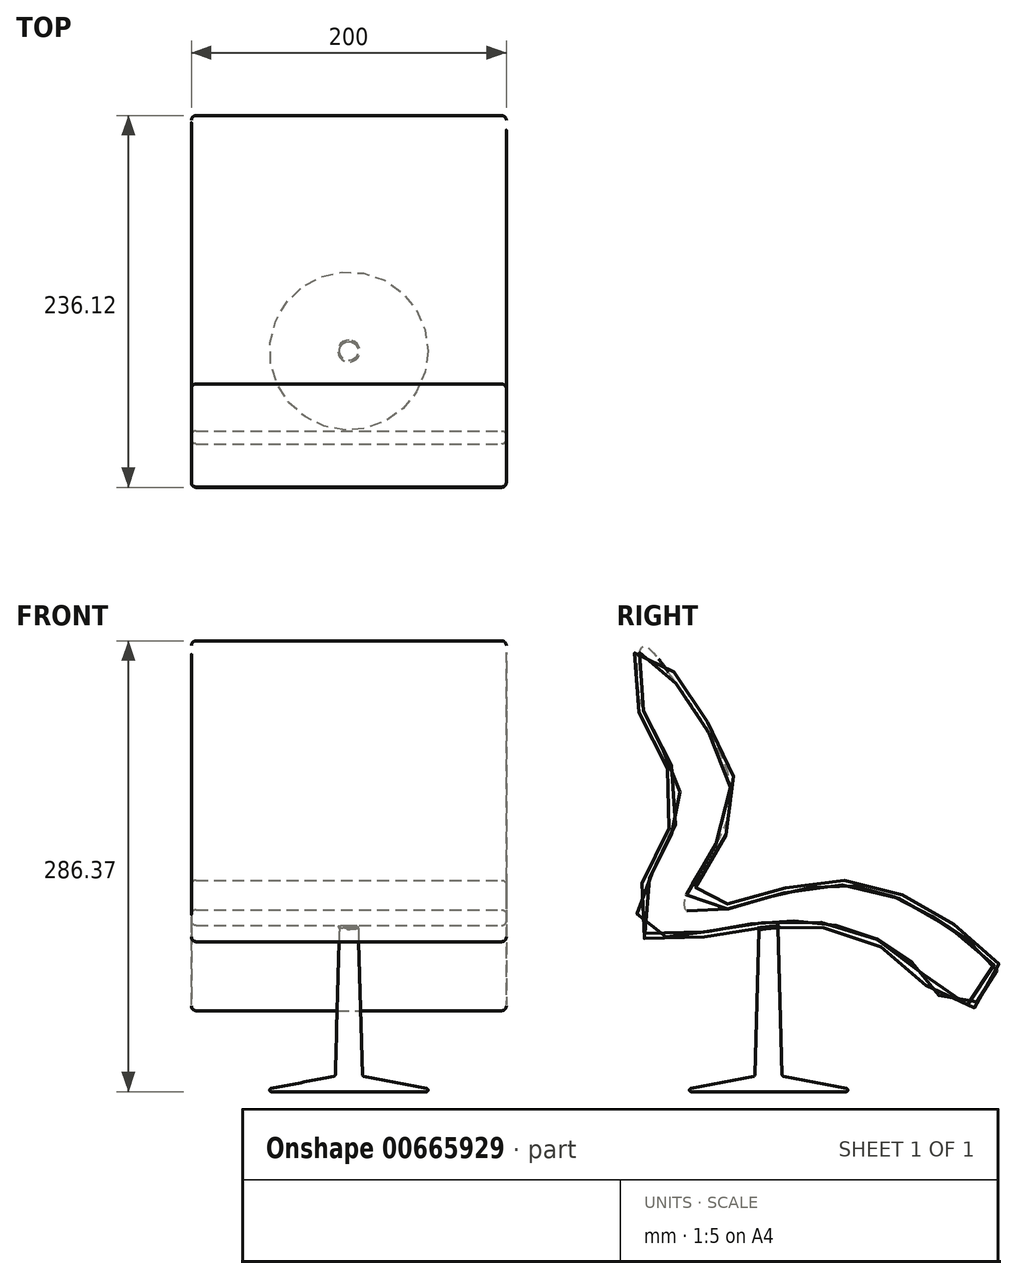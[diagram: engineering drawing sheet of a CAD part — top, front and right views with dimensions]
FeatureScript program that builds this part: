
annotation { "Feature Type Name" : "Feature", "Feature Type Description" : "" }
export const myFeature = defineFeature(function(context is Context, id is Id, definition is map)
    precondition{}
    {
        {
            var Q0;
            Q0=qCreatedBy(makeId("Top.planeOp"),FACE);
            var sketch = newSketch(context, id + "F0", { "sketchPlane" : qUnion([Q0])});
            skCircle(sketch, "E0", {"center": v(0, 0) * mm, "radius": 59.53 * mm});
            skSolve(sketch);
        }
        {
            var Q0;
            Q0=qCreatedBy(makeId("Top.planeOp"),FACE);
            cPlane(context, id + "F1", {"entities" : qUnion([Q0]), "cplaneType" : CPlaneType.OFFSET, "offset" : 10 * mm, "width" : 150 * mm, "height" : 150 * mm});
        }
        {
            var Q0;
            Q0=qCreatedBy(id+"F1.planeOp",FACE);
            var sketch = newSketch(context, id + "F2", { "sketchPlane" : qUnion([Q0])});
            skCircle(sketch, "E1", {"center": v(0, 0) * mm, "radius": 8.68 * mm});
            skSolve(sketch);
        }
        {
            var Q0;
            Q0=makeQuery(id+"F0.imprint","IMPRINT",FACE,{"disambiguationData":[TD([[makeQuery(id+"F0.imprint","IMPRINT",EDGE,{"derivedFrom":sQuery(id+"F0.wireOp",EDGE,"E0")}),1.0]])]});
            var Q1;
            Q1=makeQuery(id+"F2.imprint","IMPRINT",FACE,{"disambiguationData":[TD([[makeQuery(id+"F2.imprint","IMPRINT",EDGE,{"derivedFrom":sQuery(id+"F2.wireOp",EDGE,"E1")}),1.0]])]});
            loft(context, id + "F3", {"sheetProfilesArray" : [{ "sheetProfileEntities" : qUnion([Q0]) }, { "sheetProfileEntities" : qUnion([Q1]) }]});
        }
        {
            var Q0;
            Q0=qCreatedBy(id+"F1.planeOp",FACE);
            cPlane(context, id + "F4", {"entities" : qUnion([Q0]), "cplaneType" : CPlaneType.OFFSET, "offset" : 100 * mm, "width" : 150 * mm, "height" : 150 * mm});
        }
        {
            var Q0;
            Q0=qCreatedBy(id+"F4.planeOp",FACE);
            var sketch = newSketch(context, id + "F5", { "sketchPlane" : qUnion([Q0])});
            skCircle(sketch, "E2", {"center": v(0, 0) * mm, "radius": 5.83 * mm});
            skSolve(sketch);
        }
        {
            var Q0;
            Q0=qCreatedBy(id+"F1.planeOp",FACE);
            var sketch = newSketch(context, id + "F6", { "sketchPlane" : qUnion([Q0])});
            skCircle(sketch, "E3", {"center": v(0, 0) * mm, "radius": 8.62 * mm});
            skSolve(sketch);
        }
        {
            var Q1;
            Q1=makeQuery(id+"F6.imprint","IMPRINT",FACE,{"disambiguationData":[TD([[makeQuery(id+"F6.imprint","IMPRINT",EDGE,{"derivedFrom":sQuery(id+"F6.wireOp",EDGE,"E3")}),1.0]])]});
            var Q2;
            Q2=makeQuery(id+"F5.imprint","IMPRINT",FACE,{"disambiguationData":[TD([[makeQuery(id+"F5.imprint","IMPRINT",EDGE,{"derivedFrom":sQuery(id+"F5.wireOp",EDGE,"E2")}),1.0]])]});
            loft(context, id + "F7", {"operationType" : NewBodyOperationType.ADD, "sheetProfilesArray" : [{ "sheetProfileEntities" : qUnion([Q1]) }, { "sheetProfileEntities" : qUnion([Q2]) }]});
        }
        {
            var Q0;
            Q0=makeQuery(id+"F7.opLoft","SWEPT_FACE",FACE,{"disambiguationData":[OSD([sQuery(id+"F5.wireOp",EDGE,"E2"),sQuery(id+"F6.wireOp",EDGE,"E3")])]});
            fillet(context, id + "F8", {"entities" : qUnion([Q0]), "radius" : 1 * mm, "tangentPropagation" : true, "allowEdgeOverflow" : false});
        }
        {
            var Q0;
            Q0=makeQuery(id+"F3.opLoft","MID_CAP_EDGE",EDGE,{"disambiguationData":[OSD([sQuery(id+"F0.wireOp",EDGE,"E0")])],"capPos":0.0});
            fillet(context, id + "F9", {"entities" : qUnion([Q0]), "radius" : 1 * mm, "tangentPropagation" : true, "allowEdgeOverflow" : false});
        }
        {
            var Q0;
            {var subQ0=sQuery(id+"F6.wireOp",EDGE,"E3");Q0=makeQuery(id+"F8.opFillet","BLEND_EDGE",EDGE,{"blendedFrom":[makeQuery(id+"F7.opLoft","MID_CAP_EDGE",EDGE,{"disambiguationData":[OSD([subQ0])],"capPos":0.0}),makeQuery(id+"F7.opLoft","SWEPT_FACE",FACE,{"disambiguationData":[OSD([sQuery(id+"F5.wireOp",EDGE,"E2"),subQ0])]})],"blendedInto":[makeQuery(id+"F7.opLoft","SWEPT_FACE",FACE,{"disambiguationData":[OSD([sQuery(id+"F5.wireOp",EDGE,"E2"),subQ0])]})]});}
            var Q1;
            Q1=makeQuery(id+"F3.opLoft","SWEPT_FACE",FACE,{"disambiguationData":[OSD([sQuery(id+"F0.wireOp",EDGE,"E0"),sQuery(id+"F2.wireOp",EDGE,"E1")])]});
            fillet(context, id + "F10", {"entities" : qUnion([Q0, Q1]), "radius" : 1 * mm, "tangentPropagation" : true, "allowEdgeOverflow" : false});
        }
        {
            var Q0;
            Q0=qCreatedBy(id+"F4.planeOp",FACE);
            var sketch = newSketch(context, id + "F11", { "sketchPlane" : qUnion([Q0])});
            skCircle(sketch, "E4", {"center": v(0, 0) * mm, "radius": 104.72 * mm});
            skSolve(sketch);
        }
        {
            var Q0;
            Q0=qCreatedBy(makeId("Front.planeOp"),FACE);
            var sketch = newSketch(context, id + "F12", { "sketchPlane" : qUnion([Q0])});
            skCircle(sketch, "E5", {"center": v(-127.32, 163.74) * mm, "radius": 116.48 * mm});
            skSolve(sketch);
        }
        {
            var Q0;
            Q0=makeQuery(id+"F12.imprint","IMPRINT",FACE,{"disambiguationData":[TD([[makeQuery(id+"F12.imprint","IMPRINT",EDGE,{"derivedFrom":sQuery(id+"F12.wireOp",EDGE,"E5")}),1.0]])]});
            var Q1;
            Q1=sQuery(id+"F11.wireOp",EDGE,"E4");
            revolve(context, id + "F13", {"entities" : qUnion([Q0]), "axis" : qUnion([Q1]), "revolveType" : RevolveType.FULL});
        }
        {
            var Q0;
            Q0=makeQuery(id+"F13.opRevolve","SWEPT_BODY",BODY,{"disambiguationData":[OSD([sQuery(id+"F12.wireOp",EDGE,"E5")])]});
            deleteBodies(context, id + "F14", {"entities" : qUnion([Q0])});
        }
        {
            var Q0;
            Q0=qCreatedBy(makeId("Right.planeOp"),FACE);
            var sketch = newSketch(context, id + "F15", { "sketchPlane" : qUnion([Q0])});
            skFitSpline(sketch, "E6", {"points": [v(-87, 252.75) * mm, v(-107.33, 189.53) * mm, v(-98.96, 116.28) * mm, v(29.17, 113.43) * mm, v(97.88, 85.57) * mm, v(131.17, 15.57) * mm, v(166.8, 30) * mm, v(142.37, 102.52) * mm, v(93.03, 139.71) * mm, v(0, 140.98) * mm, v(-84.56, 144.78) * mm, v(-63.6, 254.61) * mm, v(-50.53, 315.86) * mm, v(-63.64, 345.3) * mm, v(-95.8, 317.9) * mm, v(-87, 252.75) * mm]});
            skSolve(sketch);
        }
        {
            var Q0;
            Q0 = qSketchRegion(id + "F15", true);
            extrude(context, id + "F16", {"entities" : qUnion([Q0]), "depth" : 100 * mm, "offsetDistance" : 25 * mm});
        }
        {
            var Q0;
            Q0=makeQuery(id+"F16.opExtrude","CAP_EDGE",EDGE,{"disambiguationData":[OSD([sQuery(id+"F15.wireOp",EDGE,"E6")])],"isStart":false});
            fillet(context, id + "F17", {"entities" : qUnion([Q0]), "radius" : 2 * mm, "tangentPropagation" : true, "allowEdgeOverflow" : false});
        }
        {
            var Q0;
            Q0=makeQuery(id+"F16.opExtrude","CAP_EDGE",EDGE,{"disambiguationData":[OSD([sQuery(id+"F15.wireOp",EDGE,"E6")])],"isStart":true});
            fillet(context, id + "F18", {"entities" : qUnion([Q0]), "radius" : 2 * mm, "tangentPropagation" : true, "allowEdgeOverflow" : false});
        }
        {
            var Q0;
            Q0=makeQuery(id+"F16.opExtrude","SWEPT_BODY",BODY,{"disambiguationData":[OSD([sQuery(id+"F15.wireOp",EDGE,"E6")])]});
            deleteBodies(context, id + "F19", {"entities" : qUnion([Q0])});
        }
        {
            var Q0;
            Q0=qCreatedBy(makeId("Right.planeOp"),FACE);
            var sketch = newSketch(context, id + "F20", { "sketchPlane" : qUnion([Q0])});
            skFitSpline(sketch, "E7", {"points": [v(-82.27, 240.98) * mm, v(-58.97, 185.65) * mm, v(-85.18, 120.12) * mm, v(-77.9, 96.83) * mm, v(16.74, 105.56) * mm, v(93.92, 74.99) * mm, v(117.21, 51.7) * mm, v(149.25, 69.16) * mm, v(107.02, 112.84) * mm, v(29.85, 133.23) * mm, v(-50.23, 117.21) * mm, v(-22.57, 175.45) * mm, v(-48.78, 249.71) * mm, v(-80.81, 286.12) * mm, v(-82.27, 240.98) * mm]});
            skSolve(sketch);
        }
        {
            var Q0;
            Q0 = qSketchRegion(id + "F20", true);
            extrude(context, id + "F21", {"entities" : qUnion([Q0]), "operationType" : NewBodyOperationType.ADD, "depth" : 100 * mm, "offsetDistance" : 25 * mm});
        }
        {
            var Q0;
            Q0=makeQuery(id+"F3.opLoft","SWEPT_BODY",BODY,{"disambiguationData":[OSD([makeQuery(id+"F0.imprint","IMPRINT",FACE,{"disambiguationData":[TD([[makeQuery(id+"F0.imprint","IMPRINT",EDGE,{"derivedFrom":sQuery(id+"F0.wireOp",EDGE,"E0")}),1.0]])]}),makeQuery(id+"F2.imprint","IMPRINT",FACE,{"disambiguationData":[TD([[makeQuery(id+"F2.imprint","IMPRINT",EDGE,{"derivedFrom":sQuery(id+"F2.wireOp",EDGE,"E1")}),1.0]])]})])]});
            var Q1;
            Q1=qCreatedBy(makeId("Right.planeOp"),FACE);
            mirror(context, id + "F22", {"operationType" : NewBodyOperationType.ADD, "entities" : qUnion([Q0]), "mirrorPlane" : qUnion([Q1])});
        }
        {
            var Q0;
            Q0=makeQuery(id+"F21.opExtrude","CAP_EDGE",EDGE,{"disambiguationData":[OSD([sQuery(id+"F20.wireOp",EDGE,"E7")])],"isStart":false});
            fillet(context, id + "F23", {"entities" : qUnion([Q0]), "radius" : 3 * mm, "tangentPropagation" : true, "allowEdgeOverflow" : false});
        }
        {
            var Q0;
            Q0=makeQuery(id+"F22.opPattern","COPY",EDGE,{"derivedFrom":makeQuery(id+"F21.opExtrude","CAP_EDGE",EDGE,{"disambiguationData":[OSD([sQuery(id+"F20.wireOp",EDGE,"E7")])],"isStart":false}),"instanceName":"1"});
            fillet(context, id + "F24", {"entities" : qUnion([Q0]), "radius" : 3 * mm, "tangentPropagation" : true, "allowEdgeOverflow" : false});
        }
        {
            var Q0;
            Q0=makeQuery(id+"F7.opLoft","SWEPT_FACE",FACE,{"disambiguationData":[OSD([sQuery(id+"F5.wireOp",EDGE,"E2"),sQuery(id+"F6.wireOp",EDGE,"E3")])]});
            fillet(context, id + "F25", {"entities" : qUnion([Q0]), "radius" : 1 * mm, "tangentPropagation" : true, "allowEdgeOverflow" : false});
        }
    });
